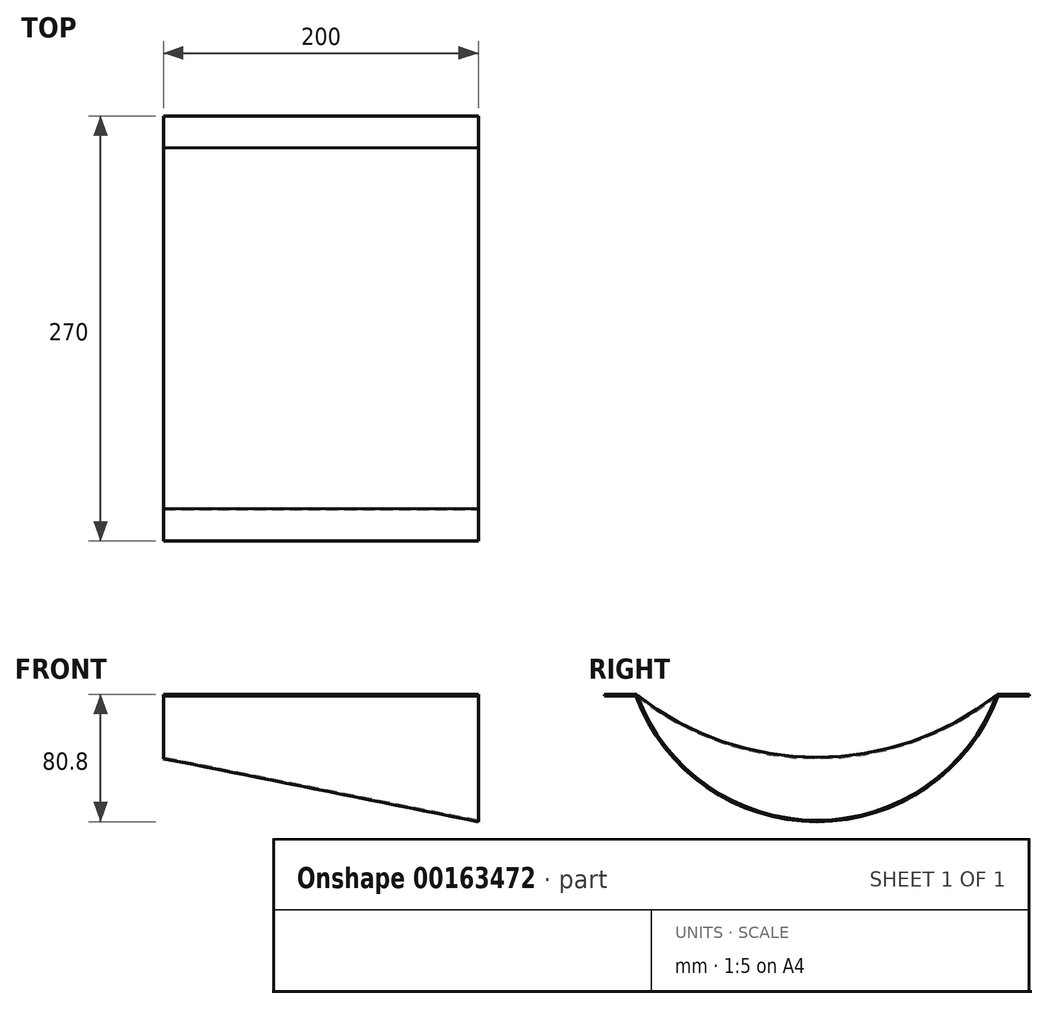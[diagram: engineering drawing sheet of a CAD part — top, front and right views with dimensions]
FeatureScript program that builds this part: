
annotation { "Feature Type Name" : "Feature", "Feature Type Description" : "" }
export const myFeature = defineFeature(function(context is Context, id is Id, definition is map)
    precondition{}
    {
        {
            var Q0;
            Q0=qCreatedBy(makeId("Right.planeOp"),FACE);
            var sketch = newSketch(context, id + "F0", { "sketchPlane" : qUnion([Q0])});
            skArc(sketch, "E0", {"start": v(-115, 0) * mm, "mid": v(0, -40) * mm, "end": v(115, 0) * mm});
            skLineSegment(sketch, "E1", {"start": v(-115, 0) * mm, "end": v(115, 0) * mm, "construction": true});
            skLineSegment(sketch, "E2", {"start": v(0, 0) * mm, "end": v(0, -40) * mm, "construction": true});
            skLineSegment(sketch, "E3", {"start": v(-115, 0) * mm, "end": v(-135, 0) * mm});
            skLineSegment(sketch, "E4", {"start": v(115, 0) * mm, "end": v(135, 0) * mm});
            skLineSegment(sketch, "E5.0", {"start": v(-114.72, 0.8) * mm, "end": v(-135, 0.8) * mm});
            skArc(sketch, "E5.1", {"start": v(-114.72, 0.8) * mm, "mid": v(0, -39.2) * mm, "end": v(114.72, 0.8) * mm});
            skLineSegment(sketch, "E5.2", {"start": v(114.72, 0.8) * mm, "end": v(135, 0.8) * mm});
            skLineSegment(sketch, "E6", {"start": v(-135, 0.8) * mm, "end": v(-135, 0) * mm});
            skLineSegment(sketch, "E7", {"start": v(135, 0.8) * mm, "end": v(135, 0) * mm});
            skSolve(sketch);
        }
        {
            var Q0;
            Q0=makeQuery(id+"F0.imprint","IMPRINT",FACE,{"disambiguationData":[TD([[makeQuery(id+"F0.imprint","IMPRINT",EDGE,{"derivedFrom":sQuery(id+"F0.wireOp",EDGE,"E0")}),1.0]])]});
            cPlane(context, id + "F1", {"entities" : qUnion([Q0]), "cplaneType" : CPlaneType.OFFSET, "offset" : 200 * mm, "width" : 150 * mm, "height" : 150 * mm});
        }
        {
            var Q0;
            Q0=qCreatedBy(id+"F1.planeOp",FACE);
            var sketch = newSketch(context, id + "F2", { "sketchPlane" : qUnion([Q0])});
            skArc(sketch, "E8", {"start": v(-115, 0) * mm, "mid": v(0, -80) * mm, "end": v(115, 0) * mm});
            skLineSegment(sketch, "E9", {"start": v(-115, 0) * mm, "end": v(-135, 0) * mm});
            skLineSegment(sketch, "E10", {"start": v(115, 0) * mm, "end": v(135, 0) * mm});
            skLineSegment(sketch, "E11.0", {"start": v(-114.44, 0.8) * mm, "end": v(-135, 0.8) * mm});
            skArc(sketch, "E11.1", {"start": v(-114.44, 0.8) * mm, "mid": v(0, -79.2) * mm, "end": v(114.44, 0.8) * mm});
            skLineSegment(sketch, "E11.2", {"start": v(114.44, 0.8) * mm, "end": v(135, 0.8) * mm});
            skLineSegment(sketch, "E12", {"start": v(-135, 0.8) * mm, "end": v(-135, 0) * mm});
            skLineSegment(sketch, "E13", {"start": v(135, 0.8) * mm, "end": v(135, 0) * mm});
            skSolve(sketch);
        }
        {
            var Q0;
            Q0=makeQuery(id+"F0.imprint","IMPRINT",FACE,{"disambiguationData":[TD([[makeQuery(id+"F0.imprint","IMPRINT",EDGE,{"derivedFrom":sQuery(id+"F0.wireOp",EDGE,"E0")}),1.0]])]});
            var Q1;
            Q1=makeQuery(id+"F2.imprint","IMPRINT",FACE,{"disambiguationData":[TD([[makeQuery(id+"F2.imprint","IMPRINT",EDGE,{"derivedFrom":sQuery(id+"F2.wireOp",EDGE,"E8")}),1.0]])]});
            var Q2;
            Q2=sQuery(id+"F0.wireOp",EDGE,"E0");
            var Q3;
            Q3=sQuery(id+"FA8bKThe5yn7DPf_0.wireOp",EDGE,"qVX898tD-mlmV-Xog1-vHix-Hoe26mr1r6RD");
            loft(context, id + "F3", {"sheetProfilesArray" : [{ "sheetProfileEntities" : qUnion([Q0]) }, { "sheetProfileEntities" : qUnion([Q1]) }], "wireProfilesArray" : [{ "wireProfileEntities" : qUnion([Q2]) }, { "wireProfileEntities" : qUnion([Q3]) }]});
        }
    });
